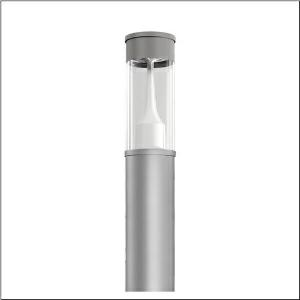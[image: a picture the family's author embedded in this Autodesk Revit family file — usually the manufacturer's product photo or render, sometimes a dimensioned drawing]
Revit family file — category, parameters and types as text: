
# Revit family: city-light_400_iq___p1_0a_5xa5305nf14hp_4342
name_source: partatom
category: Lighting Fixtures
units: mm (PartAtom-declared; Revit-internal decimal feet)

## family parameters
Cut with Voids When Loaded = No
Host = Face
Light Source = No
Part Type = Normal
Room Calculation Point = No
Round Connector Dimension = Use Diameter
Shared = No

## types (1)
- --- (1 x LED, 4210 lm, 33.6 W, 2700K)
    Apparent Load = 34 VA
    CIE Flux Codes = 31 62 91 95 100
    Color Rendering = 70
    Color Temperature = 2700K
    Default Elevation = 1800 mm
    Description = City-Light 400 iQ, light pillar, Module 540 iQ-SR, primary light control with 3 zone facetted reflector, of plastic, silver coated, highly specular, structured, primary optical cover: cover, of PMMA, transparent, partly coated, light distribution: P1.0a, primary light characteristic: strongly asymmetric, LED, High Power LED, rated luminous flux: 4.210lm, luminous efficacy: 125lm/W, light colour: 727, colour temperature: 2700K, control gear: ECG iQ, control: presetting dimming logarithmic, Street-Remote, Auto-Match, Temp-Guard, Lumen-Switch, Night-Set, Smart-Wire, Light-Fading, Desk-Remote (wireless, voltage-free reading and setting of iQ features in the workshop via application-optimized NFC function/RFID function), optimised constant luminous flux control (CLO 2.0), with terminal, 6-pole, max. 2.5mm², mains connection: 230..240V, AC, 50/60Hz, start of lifetime: 34W, end of service life: 36W, reduction: 15W, luminaire housing, cylindrical, of extruded aluminium section, coated, Siteco® metallic grey (DB 702S), length: 4.694mm, diameter: 200mm, Module 540 iQ-SR, traffic white (RAL 9016), equipment: Power, protection rating (complete): IP65, insulation class (complete): insulation class II (safety insulation), certification: CE, ENEC, VDE, packaging unit: 1 piece

Light Distribution: P1.0a
    Height = 500 mm
    Lamp = 1 x LED
    Lamp Light Flux = 4210 lm
    Lamp Power = 33.6 W
    Lamp count = 1
    Length = 200 mm
    Luminous efficacy = 125 lm/W
    Manufacturer = Siteco
    ModVariant = No
    Model = 5XA5305NF14HP
    Mounting Place = Floor
    Mounting Type = Freestanding
    Number of Poles = 1
    OnlyDefault = Yes
    Power Factor = 1
    Product Name = City-Light 400 iQ | P1.0a
    Product group = light pillar
    ProductGroupID = 1303
    Protection Class = Protection class II
    Protection Degree = IP 65
    RLX_Detail_Level = 1
    RLX_Emergency_Light_Flux = 0 lm
    RLX_Emergency_Type = 0
    RLX_Emergency_Type_DB = No
    RlxData = <blob elided: 53597 chars, md5=958415ae>
    Socket = socket
    Standby Power = 0 W
    System Light Flux = 4210 lm
    System Power = 34 W
    Type Comments = factory setting: luminous flux: 100 % | dim-lin: 254 | 695 mA
    Type Image = l_1006916.jpg
    URL = http://relux.com
    VarID = @adj_084769
    Voltage = 0 V
    Weight = 0.00 kg
    Width = 0 mm  [stored 0 ft]

note: [stored X ft] marks values corroborated as IEEE doubles in the binary element streams (Revit-internal decimal feet)

## geometry (parser evidence)
native form markers: Blend x4, Sweep x10
no freeform markers — native parametric forms only
